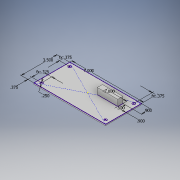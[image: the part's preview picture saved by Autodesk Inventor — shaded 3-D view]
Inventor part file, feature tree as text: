
AUTODESK INVENTOR PART (.ipt)
format: ipt  version: 2018 (Build 220112000, 112)  size: 116,224 bytes
history: native  units: in
note: dims shown in document units (in); Inventor stores cm internally (conversion verified against a paired STEP export)
features: sketch x2, extrude x2
ambient origin geometry x8: Origin, YZ Plane, XZ Plane, XY Plane, X Axis, Y Axis, Z Axis, Center Point
bodies: Solid1 (feature_tree)
feature tree (4):
  sketch  "Sketch1"  dims[d0=7.0in d1=3.5in]
  extrude  "Extrusion1"  Depth=3.5in
  extrude  "Extrusion2"  Depth=0.9in
  sketch  "Sketch2"  dims[d2=0.9in d3=0.9in d4=0.5in d5=2.0in d6=0.125in d7=0.0in d8=0.6in d9=0.0in d10=0.375in d11=0.375in d12=0.375in d13=0.375in d14=0.25in]
